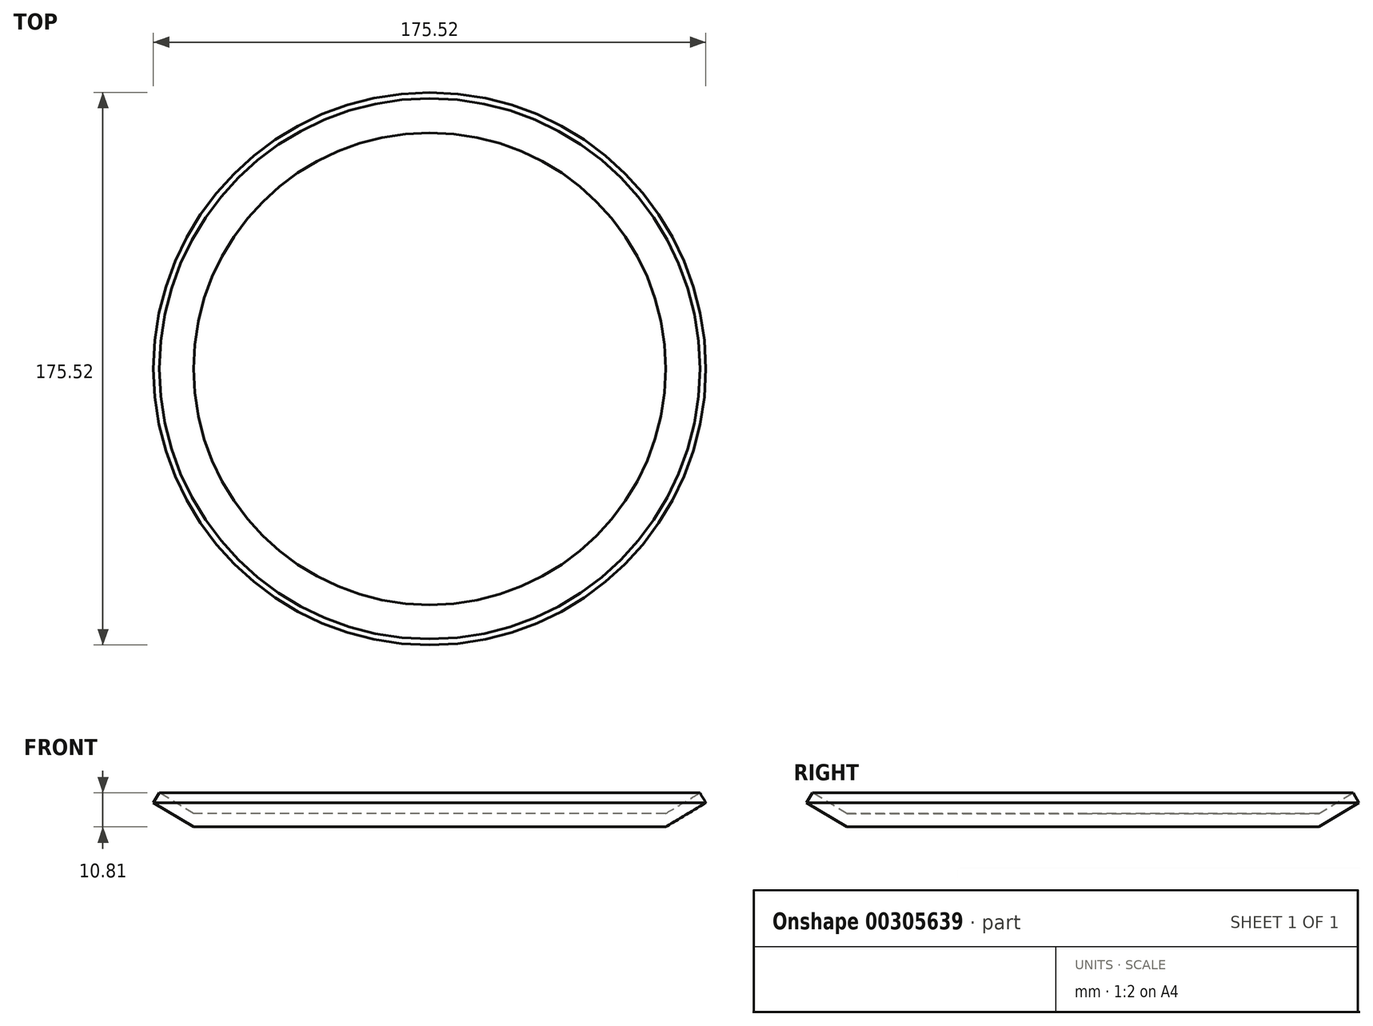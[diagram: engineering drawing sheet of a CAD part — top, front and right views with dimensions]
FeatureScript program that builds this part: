
annotation { "Feature Type Name" : "Feature", "Feature Type Description" : "" }
export const myFeature = defineFeature(function(context is Context, id is Id, definition is map)
    precondition{}
    {
        {
            var Q0;
            Q0=qCreatedBy(makeId("Front.planeOp"),FACE);
            var sketch = newSketch(context, id + "F0", { "sketchPlane" : qUnion([Q0])});
            skLineSegment(sketch, "E0", {"start": v(0, 0) * mm, "end": v(75, 0) * mm});
            skLineSegment(sketch, "E1", {"start": v(75, 0) * mm, "end": v(87.76, 7.67) * mm});
            skLineSegment(sketch, "E2", {"start": v(87.76, 7.67) * mm, "end": v(85.87, 10.8) * mm});
            skLineSegment(sketch, "E3", {"start": v(85.87, 10.8) * mm, "end": v(75, 4.27) * mm});
            skLineSegment(sketch, "E4", {"start": v(75, 4.27) * mm, "end": v(0, 4.27) * mm});
            skLineSegment(sketch, "E5", {"start": v(0, 4.27) * mm, "end": v(0, 0) * mm});
            skSolve(sketch);
        }
        {
            var Q0;
            Q0=makeQuery(id+"F0.imprint","IMPRINT",FACE,{"disambiguationData":[TD([[makeQuery(id+"F0.imprint","IMPRINT",EDGE,{"derivedFrom":sQuery(id+"F0.wireOp",EDGE,"E0")}),1.0]])]});
            var Q1;
            Q1=sQuery(id+"F0.wireOp",EDGE,"E5");
            revolve(context, id + "F1", {"entities" : qUnion([Q0]), "axis" : qUnion([Q1]), "revolveType" : RevolveType.FULL});
        }
    });
